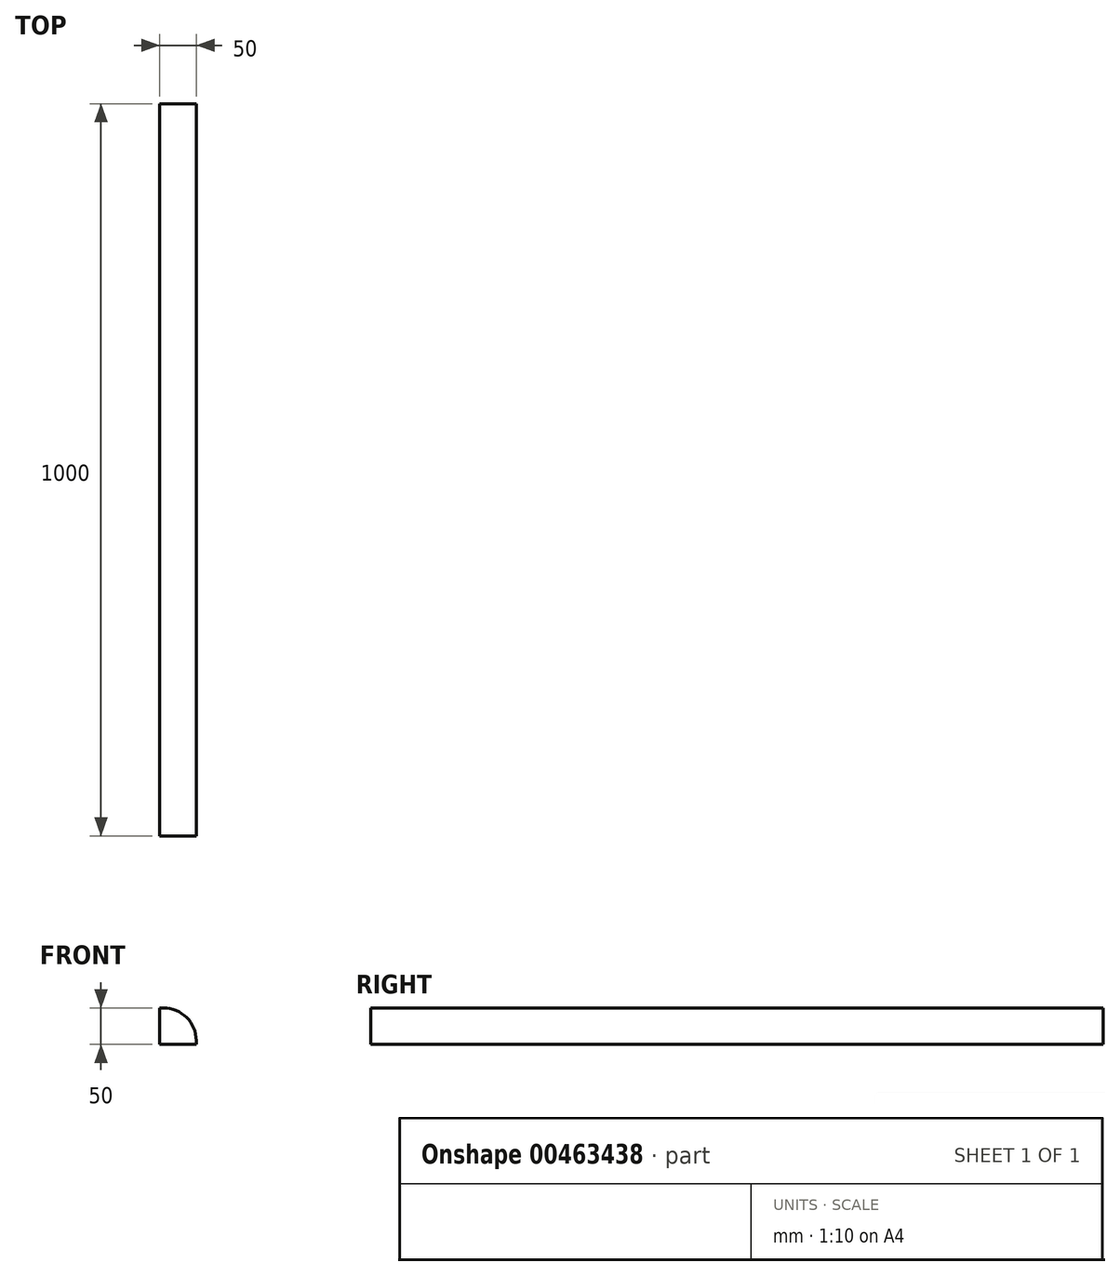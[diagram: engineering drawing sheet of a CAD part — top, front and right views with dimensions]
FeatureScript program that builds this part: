
annotation { "Feature Type Name" : "Feature", "Feature Type Description" : "" }
export const myFeature = defineFeature(function(context is Context, id is Id, definition is map)
    precondition{}
    {
        {
            var Q0;
            Q0=qCreatedBy(makeId("Front.planeOp"),FACE);
            var sketch = newSketch(context, id + "F0", { "sketchPlane" : qUnion([Q0])});
            skLineSegment(sketch, "E0", {"start": v(0, 0) * mm, "end": v(50, 0) * mm});
            skLineSegment(sketch, "E1", {"start": v(0, 0) * mm, "end": v(0, 50) * mm});
            skLineSegment(sketch, "E2", {"start": v(0, 50) * mm, "end": v(5, 50) * mm});
            skLineSegment(sketch, "E3", {"start": v(50, 5) * mm, "end": v(50, 0) * mm});
            skPoint(sketch, "E4.visualSharp", {"position": v(50, 50) * mm});
            skArc(sketch, "E4.filletArc", {"start": v(50, 5) * mm, "mid": v(36.82, 36.82) * mm, "end": v(5, 50) * mm});
            skSolve(sketch);
        }
        {
            var Q0;
            Q0=makeQuery(id+"F0.imprint","IMPRINT",FACE,{"disambiguationData":[TD([[makeQuery(id+"F0.imprint","IMPRINT",EDGE,{"derivedFrom":sQuery(id+"F0.wireOp",EDGE,"E0")}),1.0]])]});
            extrude(context, id + "F1", {"entities" : qUnion([Q0]), "oppositeDirection" : true, "depth" : 1000 * mm});
        }
    });
